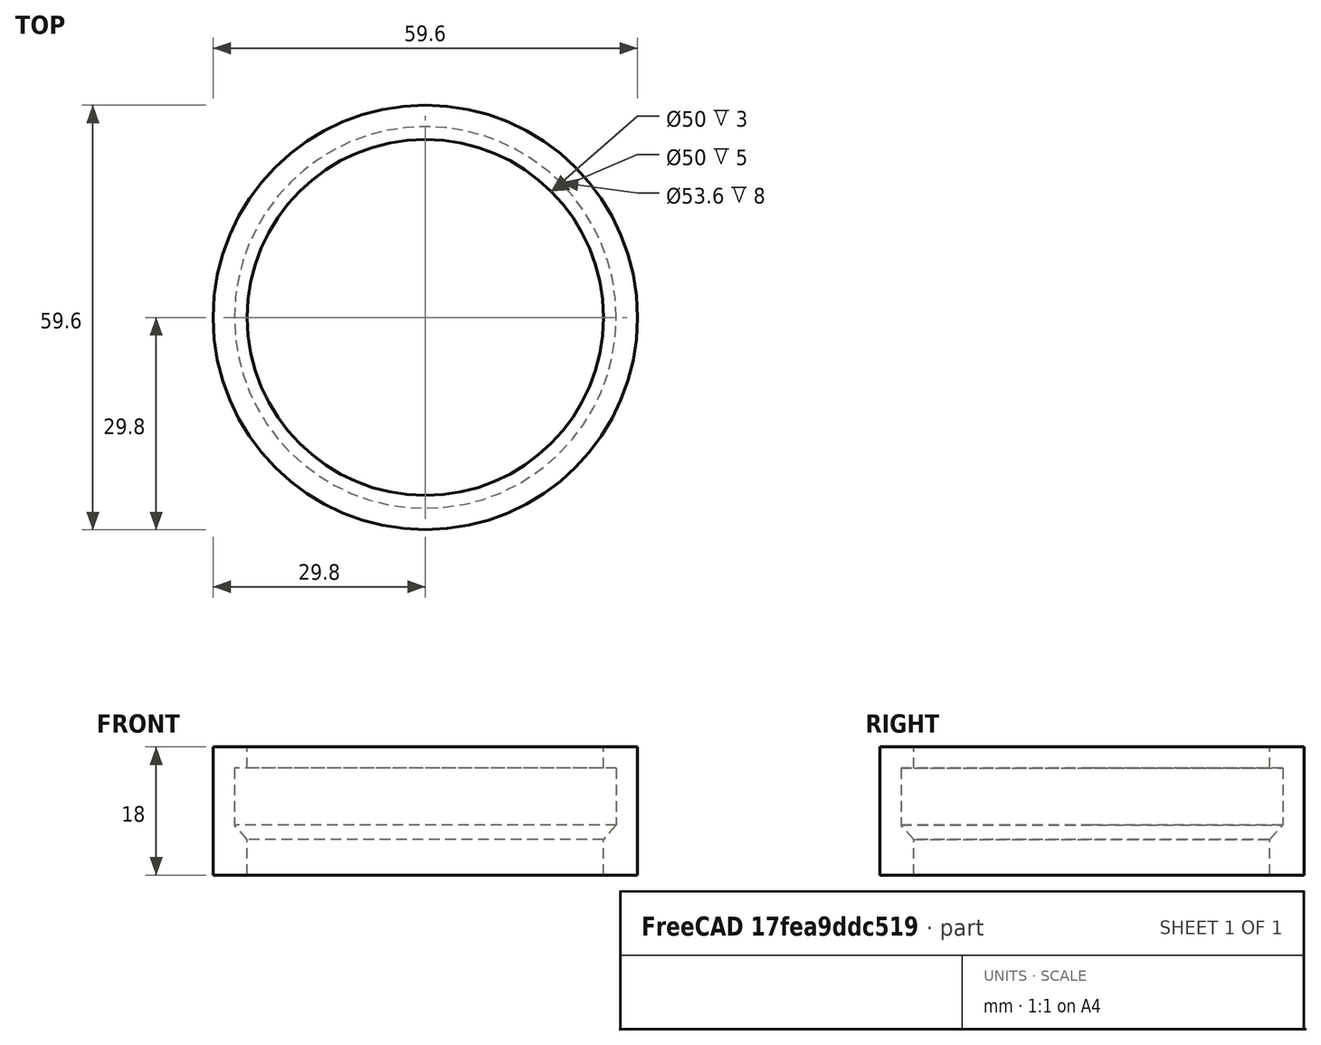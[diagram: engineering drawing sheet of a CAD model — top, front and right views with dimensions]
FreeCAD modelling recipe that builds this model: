
FCSTD DOCUMENT  (FreeCAD 1.1R39748 (Git))
Label: горло
License: All rights reserved
LicenseURL: https://en.wikipedia.org/wiki/All_rights_reserved
objects: App::Point×1, Sketcher::SketchObject×1, PartDesign::Revolution×1, PartDesign::Body×1
note: 6 computed .brp shape members not serialized (recipe doc carries the construction recipe); baked Part::Feature solids carry a one-line shape summary decoded from their .brp

FEATURE [App::Point] Origin001
  Role = Origin
FEATURE [Sketcher::SketchObject] Sketch
  ArcFitTolerance = 1e-06
  AttachmentSupport = -> [XZ_Plane]
  ExternalTypes = [0]
  FullyConstrained = true
  MakeInternals = false
  MapMode = 5
  Placement = pos=(0,0,0) rot=(1,0,0;1.5708rad)
  expr: Constraints[2] = 50 / 2
  expr: Constraints[8] = (50 + 1.8 * 2) / 2
  sketch-geometry (8):
    g0: LineSegment StartX=25 StartY=0 StartZ=0 EndX=25 EndY=5 EndZ=0
    g1: LineSegment StartX=26.8 StartY=15 StartZ=0 EndX=26.8 EndY=7 EndZ=0
    g2: LineSegment StartX=26.8 StartY=7 StartZ=0 EndX=25 EndY=5 EndZ=0
    g3: LineSegment StartX=26.8 StartY=15 StartZ=0 EndX=25 EndY=15 EndZ=0
    g4: LineSegment StartX=25 StartY=15 StartZ=0 EndX=25 EndY=18 EndZ=0
    g5: LineSegment StartX=25 StartY=18 StartZ=0 EndX=29.8 EndY=18 EndZ=0
    g6: LineSegment StartX=29.8 StartY=18 StartZ=0 EndX=29.8 EndY=0 EndZ=0
    g7: LineSegment StartX=29.8 StartY=0 StartZ=0 EndX=25 EndY=0 EndZ=0
  constraints (24):
    c: PointOnObject(g0,g-1)
    c: Vertical(g0)
    c: Distance(g0,g-1) = 25
    c: Vertical(g1)
    c: Coincident(g2,g0)
    c: DistanceY(g0,g2) = 2
    c: Coincident(g1,g2)
    c: Distance(g1,g1) = 8
    c: DistanceX(g-1,g1) = 26.8
    c: Coincident(g3,g1)
    c: Horizontal(g3)
    c: DistanceX(g-1,g3) = 25
    c: Coincident(g4,g3)
    c: Vertical(g4)
    c: Coincident(g5,g4)
    c: Horizontal(g5)
    c: Coincident(g6,g5)
    c: PointOnObject(g6,g-1)
    c: Vertical(g6)
    c: Coincident(g7,g6)
    c: Coincident(g7,g0)
    c: Distance(g3,g4) = 3
    c: DistanceX(g1,g6) = 3
    c: DistanceY(g0,g0) = 5
FEATURE [PartDesign::Revolution] Revolution
  Angle = 360
  Angle2 = 60
  Axis = (0,2e-16,1)
  Base = (0,0,0)
  Placement = pos=(0,0,0) rot=(1,0,0;1.5708rad)
  Profile = -> Sketch
  ReferenceAxis = -> Sketch [V_Axis]
  Reversed = true
  Suppressed = false
  Type = 0
FEATURE [PartDesign::Body] Body
  AllowCompound = false
  Group = -> [Sketch,Revolution]
  Origin = -> Origin
  Tip = -> Revolution
